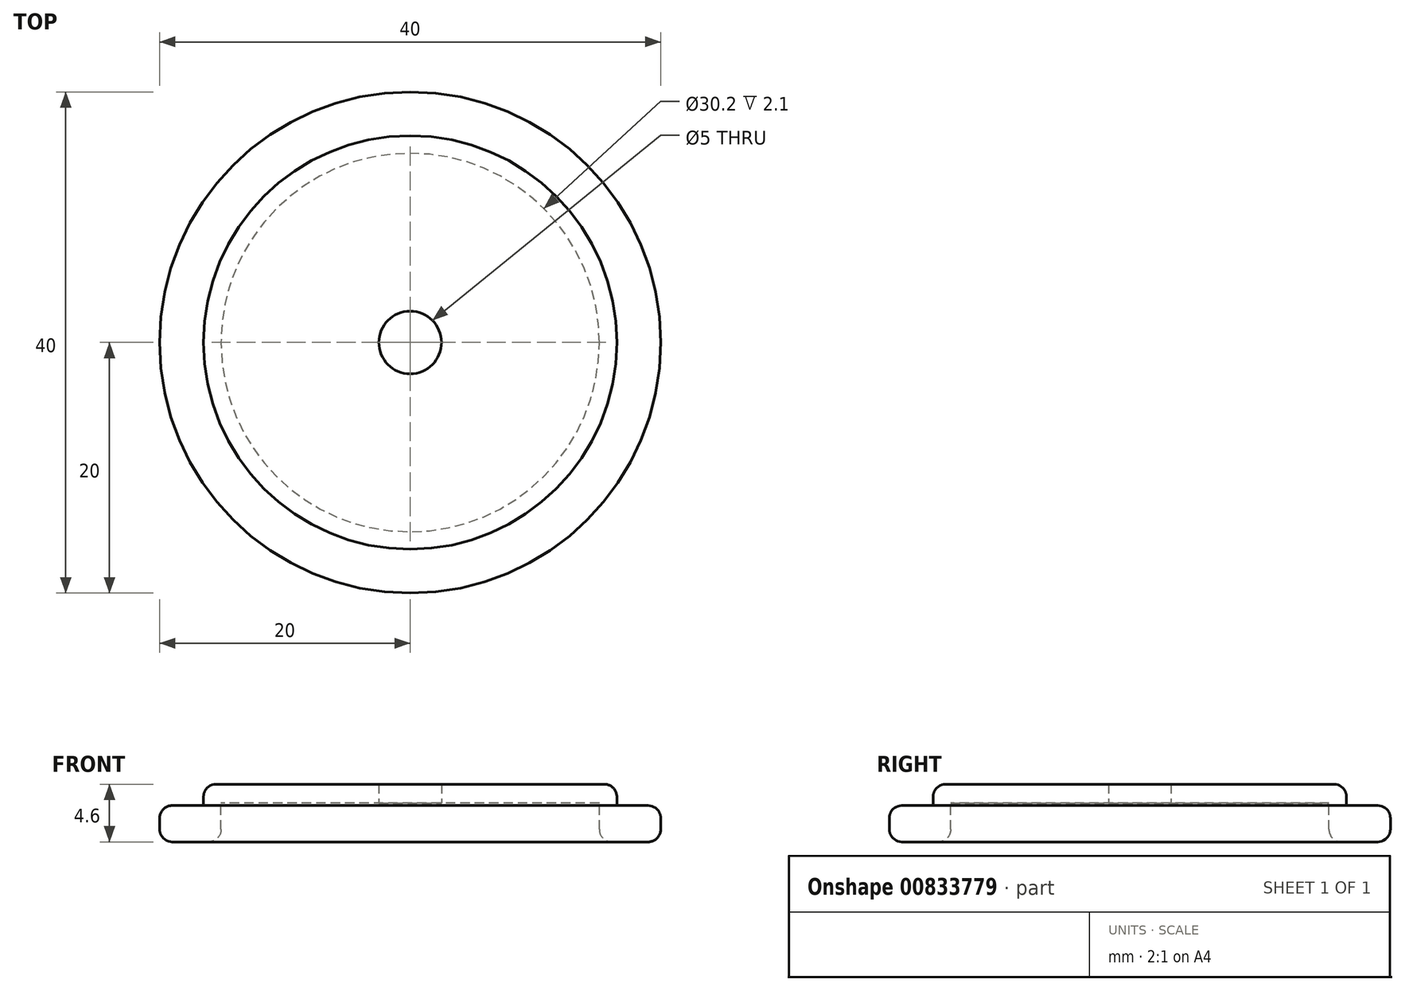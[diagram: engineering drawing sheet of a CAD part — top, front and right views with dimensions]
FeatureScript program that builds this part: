
annotation { "Feature Type Name" : "Feature", "Feature Type Description" : "" }
export const myFeature = defineFeature(function(context is Context, id is Id, definition is map)
    precondition{}
    {
        {
            var Q0;
            Q0=qCreatedBy(makeId("Front.planeOp"),FACE);
            var sketch = newSketch(context, id + "F0", { "sketchPlane" : qUnion([Q0])});
            skLineSegment(sketch, "E0.bottom", {"start": v(15.1, 0) * mm, "end": v(20, 0) * mm});
            skLineSegment(sketch, "E0.top", {"start": v(0, 3.1) * mm, "end": v(15.1, 3.1) * mm});
            skLineSegment(sketch, "E0.left", {"start": v(0, 0) * mm, "end": v(0, 3.1) * mm});
            skLineSegment(sketch, "E1.top", {"start": v(0, 4.6) * mm, "end": v(16.5, 4.6) * mm});
            skLineSegment(sketch, "E1.left", {"start": v(0, 3.1) * mm, "end": v(0, 4.6) * mm});
            skLineSegment(sketch, "E2.right", {"start": v(15.1, 0) * mm, "end": v(15.1, 3.1) * mm});
            skLineSegment(sketch, "E3", {"start": v(0, 13.04) * mm, "end": v(0, -6.9) * mm, "construction": true});
            skLineSegment(sketch, "E4", {"start": v(20, 0) * mm, "end": v(20, 2.9) * mm});
            skLineSegment(sketch, "E5", {"start": v(20, 2.9) * mm, "end": v(16.5, 2.9) * mm});
            skLineSegment(sketch, "E6", {"start": v(16.5, 2.9) * mm, "end": v(16.5, 4.6) * mm});
            skSolve(sketch);
        }
        {
            var Q0;
            Q0 = qSketchRegion(id + "F0", true);
            var Q1;
            Q1=sQuery(id+"F0.wireOp",EDGE,"E3");
            revolve(context, id + "F1", {"surfaceOperationType" : NewSurfaceOperationType.NEW, "entities" : qUnion([Q0]), "axis" : qUnion([Q1]), "revolveType" : RevolveType.FULL});
        }
        {
            var Q0;
            Q0=makeQuery(id+"F1.opRevolve","SWEPT_FACE",FACE,{"disambiguationData":[OSD([sQuery(id+"F0.wireOp",EDGE,"E0.bottom")])]});
            var Q1;
            Q1=makeQuery(id+"F1.opRevolve","SWEPT_FACE",FACE,{"disambiguationData":[OSD([sQuery(id+"F0.wireOp",EDGE,"E1.top")])]});
            var Q2;
            Q2=makeQuery(id+"F1.opRevolve","SWEPT_FACE",FACE,{"disambiguationData":[OSD([sQuery(id+"F0.wireOp",EDGE,"c9588795-47aa-46b4-8eb0-0a67026e37bd.trimOffspring")])]});
            var Q3;
            Q3=makeQuery(id+"F1.opRevolve","SWEPT_EDGE",EDGE,{"disambiguationData":[OSD([sQuery(id+"F0.wireOp",EDGE,"E4"),sQuery(id+"F0.wireOp",EDGE,"E5")])]});
            fillet(context, id + "F2", {"entities" : qUnion([Q0, Q1, Q2, Q3]), "tangentPropagation" : true, "radius" : 1 * mm, "defaultsChanged" : false, "vertexSettings" : [], "allowEdgeOverflow" : false});
        }
        {
            var Q0;
            Q0=makeQuery(id+"F1.opRevolve","SWEPT_FACE",FACE,{"disambiguationData":[OSD([sQuery(id+"F0.wireOp",EDGE,"E0.top")])]});
            var sketch = newSketch(context, id + "F3", { "sketchPlane" : qUnion([Q0])});
            skCircle(sketch, "E7", {"center": v(0, 0) * mm, "radius": 2.5 * mm});
            skSolve(sketch);
        }
        {
            var Q0;
            Q0 = qSketchRegion(id + "F3", true);
            extrude(context, id + "F4", {"entities" : qUnion([Q0]), "operationType" : NewBodyOperationType.REMOVE, "endBound" : BoundingType.THROUGH_ALL, "oppositeDirection" : true, "depth" : 25 * mm, "offsetDistance" : 25 * mm});
        }
    });
